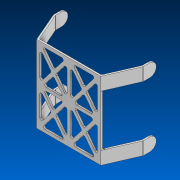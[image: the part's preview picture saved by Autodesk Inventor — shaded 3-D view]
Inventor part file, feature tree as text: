
AUTODESK INVENTOR PART (.ipt)
format: ipt  version: 2022 (Build 260153000, 153)  size: 345,600 bytes
history: native  units: in
note: dims shown in document units (in); Inventor stores cm internally (conversion verified against a paired STEP export)
features: fillet x3, extrude x2, sketch x2, mirror x1, projected_geometry x1
ambient origin geometry x8: Origin, YZ Plane, XZ Plane, XY Plane, X Axis, Y Axis, Z Axis, Center Point
bodies: Solid1 (feature_tree)
feature tree (9):
  extrude  "Extrusion1"  Depth=0.125in
  fillet  "Fillet1"  Radius=0.125in
  extrude  "Extrusion2"  Depth=0.125in
  fillet  "Fillet2"  Radius=0.125in
  fillet  "Fillet3"  Radius=0.125in
  mirror  "Mirror1"
  sketch  "Sketch1"  dims[d0=5.0in d1=6.0in d2=0.125in d3=0.0in]
  sketch  "Sketch2"  dims[d4=0.25in d5=0.125in d6=0.125in d7=0.125in d8=0.125in d9=0.125in d10=0.125in d11=0.125in d12=1.0in d13=2.3125in d14=0.125in d15=7.0in d16=0.125in d17=0.125in d18=1.0in d19=0.0in d20=0.15in d21=0.05in d22=0.5in]
  projected_geometry  "Projected Loop1"
